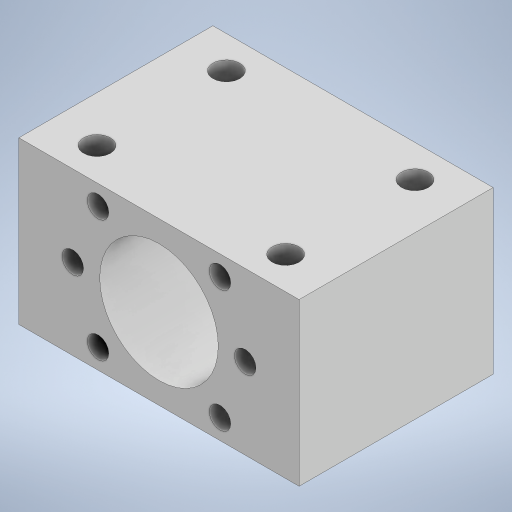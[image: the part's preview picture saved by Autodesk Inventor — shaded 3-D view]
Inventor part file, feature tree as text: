
AUTODESK INVENTOR PART (.ipt)
format: ipt  version: 2023 (Build 270158000, 158)  size: 242,688 bytes
history: native  units: mm
features: extrude x3, sketch x3
ambient origin geometry x8: Origin, YZ Plane, XZ Plane, XY Plane, X Axis, Y Axis, Z Axis, Center Point
bodies: Solid1 (feature_tree)
feature tree (6):
  extrude  "Extrusion1"  Depth=52.0mm
  extrude  "Extrusion2"  Depth=4.0mm
  extrude  "Extrusion3"  Depth=10.0mm
  sketch  "Sketch1"  dims[d0=22.0mm d2=52.0mm]
  sketch  "Sketch2"  dims[d3=32.0mm d4=4.0mm]
  sketch  "Sketch3"  dims[d5=45.0deg d6=15.0mm d9=36.0mm d10=0.0mm d11=5.0mm d12=40.0mm d13=24.0mm d14=10.0mm d15=0.0mm d16=30.0mm d17=5.0mm d18=35.0mm d19=24.0mm d20=10.0mm d21=0.0mm]
